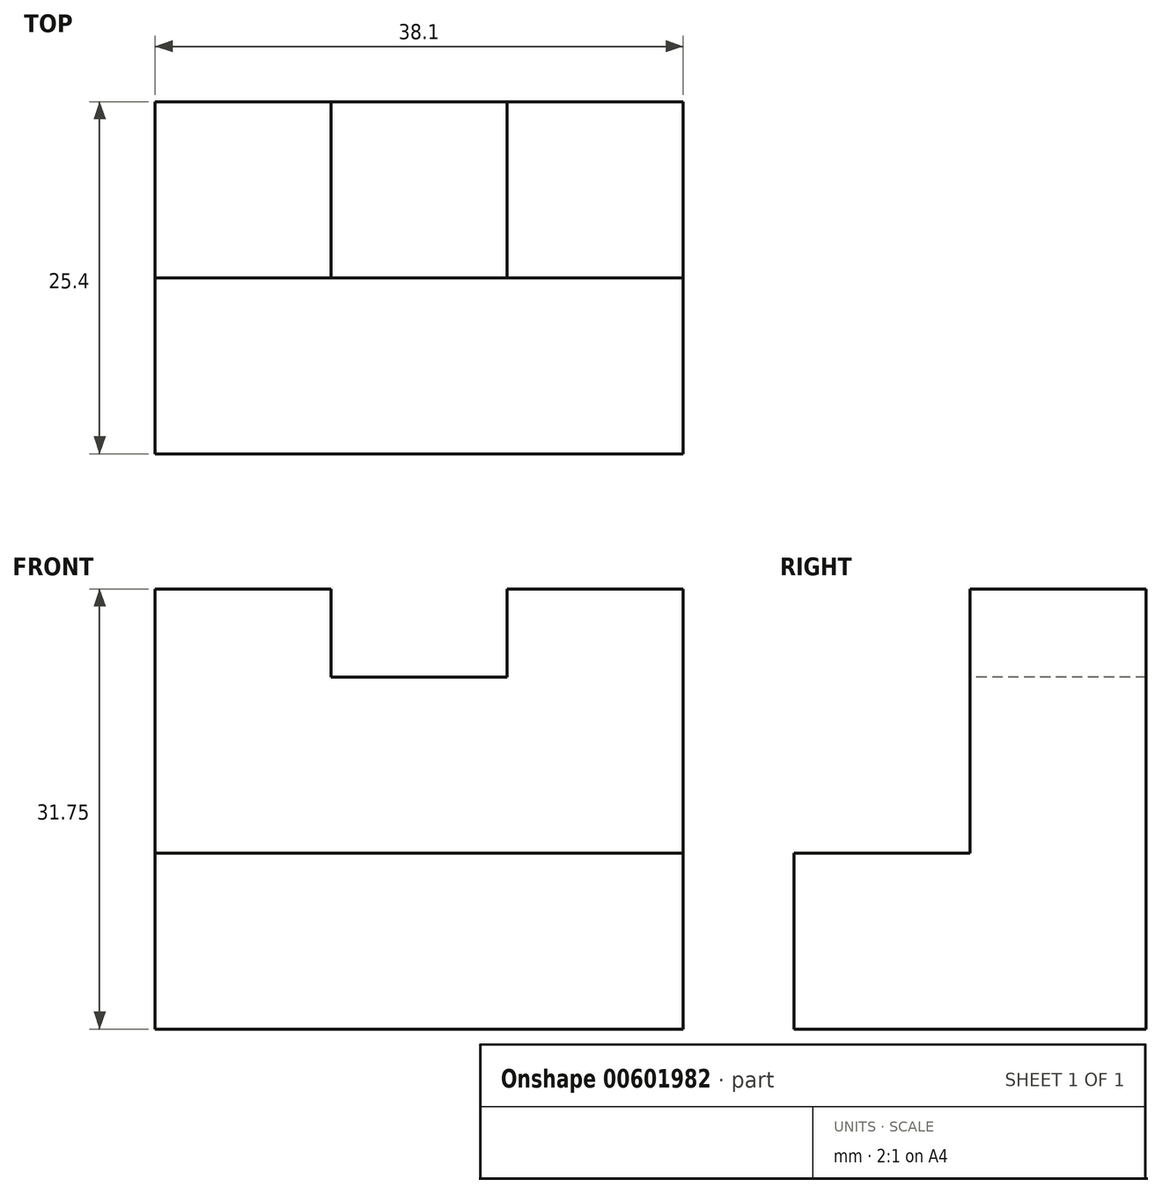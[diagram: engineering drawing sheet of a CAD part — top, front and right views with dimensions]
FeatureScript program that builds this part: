
annotation { "Feature Type Name" : "Feature", "Feature Type Description" : "" }
export const myFeature = defineFeature(function(context is Context, id is Id, definition is map)
    precondition{}
    {
        {
            var Q0;
            Q0=qCreatedBy(makeId("Right.planeOp"),FACE);
            var sketch = newSketch(context, id + "F0", { "sketchPlane" : qUnion([Q0])});
            skLineSegment(sketch, "E0", {"start": v(0, 0) * mm, "end": v(0, 31.75) * mm});
            skLineSegment(sketch, "E1", {"start": v(0, 31.75) * mm, "end": v(-12.7, 31.75) * mm});
            skLineSegment(sketch, "E2", {"start": v(-12.7, 31.75) * mm, "end": v(-12.7, 12.7) * mm});
            skLineSegment(sketch, "E3", {"start": v(-12.7, 12.7) * mm, "end": v(-25.4, 12.7) * mm});
            skLineSegment(sketch, "E4", {"start": v(-25.4, 12.7) * mm, "end": v(-25.4, 0) * mm});
            skLineSegment(sketch, "E5", {"start": v(-25.4, 0) * mm, "end": v(0, 0) * mm});
            skSolve(sketch);
        }
        {
            var Q0;
            Q0 = qSketchRegion(id + "F0", true);
            extrude(context, id + "F1", {"entities" : qUnion([Q0]), "depth" : 38.1 * mm, "offsetDistance" : 25.4 * mm});
        }
        {
            var Q0;
            Q0=makeQuery(id+"F1.opExtrude","SWEPT_FACE",FACE,{"disambiguationData":[OSD([sQuery(id+"F0.wireOp",EDGE,"E1")])]});
            var sketch = newSketch(context, id + "F2", { "sketchPlane" : qUnion([Q0])});
            skLineSegment(sketch, "E6", {"start": v(12.7, 0) * mm, "end": v(12.7, -12.7) * mm});
            skLineSegment(sketch, "E7.bottom", {"start": v(12.7, -12.7) * mm, "end": v(25.4, -12.7) * mm});
            skLineSegment(sketch, "E7.top", {"start": v(12.7, 0) * mm, "end": v(25.4, 0) * mm});
            skLineSegment(sketch, "E7.left", {"start": v(12.7, -12.7) * mm, "end": v(12.7, 0) * mm});
            skLineSegment(sketch, "E7.right", {"start": v(25.4, -12.7) * mm, "end": v(25.4, 0) * mm});
            skSolve(sketch);
        }
        {
            var Q0;
            Q0 = qSketchRegion(id + "F2", true);
            extrude(context, id + "F3", {"entities" : qUnion([Q0]), "operationType" : NewBodyOperationType.REMOVE, "oppositeDirection" : true, "depth" : 6.35 * mm, "offsetDistance" : 25.4 * mm});
        }
    });
